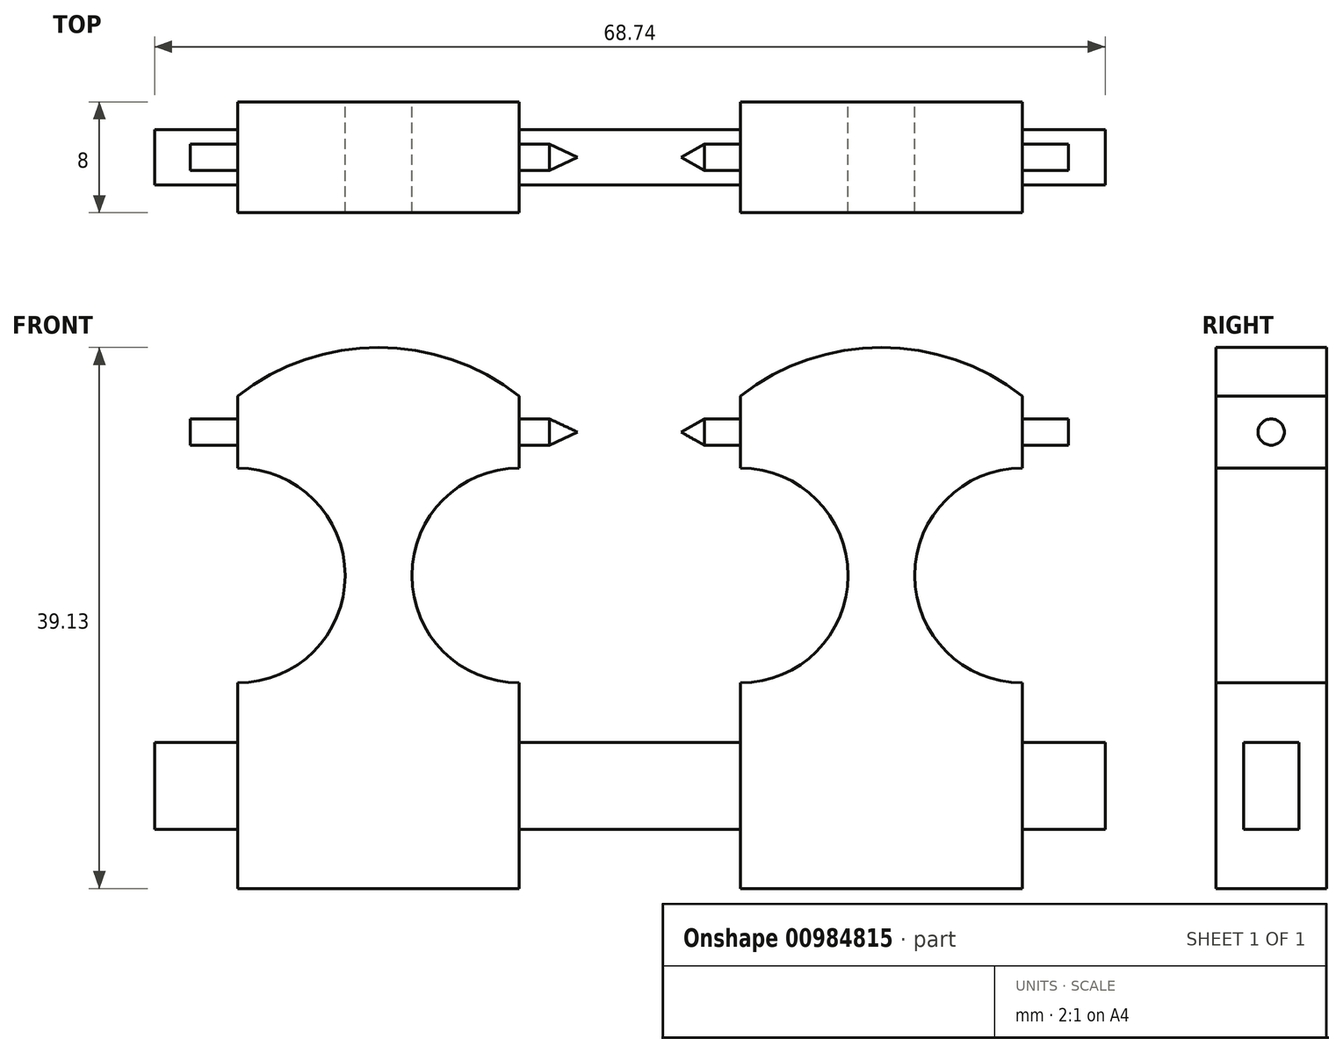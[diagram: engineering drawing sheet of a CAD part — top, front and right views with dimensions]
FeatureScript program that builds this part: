
annotation { "Feature Type Name" : "Feature", "Feature Type Description" : "" }
export const myFeature = defineFeature(function(context is Context, id is Id, definition is map)
    precondition{}
    {
        {
            var Q0;
            Q0=qCreatedBy(makeId("Front.planeOp"),FACE);
            var sketch = newSketch(context, id + "F0", { "sketchPlane" : qUnion([Q0])});
            skLineSegment(sketch, "E0", {"start": v(-34.37, 3.05) * mm, "end": v(-34.37, -3.23) * mm});
            skLineSegment(sketch, "E1", {"start": v(-34.37, -3.23) * mm, "end": v(-28.37, -3.23) * mm});
            skLineSegment(sketch, "E2", {"start": v(-28.37, -3.23) * mm, "end": v(-28.37, -7.5) * mm});
            skLineSegment(sketch, "E3", {"start": v(-28.37, -7.5) * mm, "end": v(-8, -7.5) * mm});
            skLineSegment(sketch, "E4", {"start": v(-8, -7.5) * mm, "end": v(-8, -3.23) * mm});
            skLineSegment(sketch, "E5", {"start": v(-8, -3.23) * mm, "end": v(8, -3.23) * mm});
            skLineSegment(sketch, "E6", {"start": v(8, -3.23) * mm, "end": v(8, -7.5) * mm});
            skLineSegment(sketch, "E7", {"start": v(8, -7.5) * mm, "end": v(28.37, -7.5) * mm});
            skLineSegment(sketch, "E8", {"start": v(28.37, -7.5) * mm, "end": v(28.37, -3.23) * mm});
            skLineSegment(sketch, "E9", {"start": v(28.37, -3.23) * mm, "end": v(34.37, -3.23) * mm});
            skLineSegment(sketch, "E10", {"start": v(34.37, -3.23) * mm, "end": v(34.37, 3.05) * mm});
            skLineSegment(sketch, "E11", {"start": v(34.37, 3.05) * mm, "end": v(28.37, 3.05) * mm});
            skLineSegment(sketch, "E12", {"start": v(28.37, 3.05) * mm, "end": v(28.37, 7.35) * mm});
            skLineSegment(sketch, "E13", {"start": v(-34.37, 3.05) * mm, "end": v(-28.37, 3.05) * mm});
            skLineSegment(sketch, "E14", {"start": v(-28.37, 3.05) * mm, "end": v(-28.37, 7.35) * mm});
            skLineSegment(sketch, "E15", {"start": v(-8, 7.35) * mm, "end": v(-8, 3.05) * mm});
            skLineSegment(sketch, "E16", {"start": v(-8, 3.05) * mm, "end": v(8, 3.05) * mm});
            skLineSegment(sketch, "E17", {"start": v(8, 3.05) * mm, "end": v(8, 7.35) * mm});
            skArc(sketch, "E18", {"start": v(-28.37, 7.35) * mm, "mid": v(-20.6, 15.12) * mm, "end": v(-28.37, 22.9) * mm});
            skArc(sketch, "E19", {"start": v(-8, 22.9) * mm, "mid": v(-15.77, 15.12) * mm, "end": v(-8, 7.35) * mm});
            skArc(sketch, "E20", {"start": v(8, 7.35) * mm, "mid": v(15.77, 15.12) * mm, "end": v(8, 22.9) * mm});
            skArc(sketch, "E21", {"start": v(28.37, 22.9) * mm, "mid": v(20.6, 15.12) * mm, "end": v(28.37, 7.35) * mm});
            skLineSegment(sketch, "E22", {"start": v(-28.37, 22.9) * mm, "end": v(-28.37, 28.1) * mm});
            skLineSegment(sketch, "E23", {"start": v(-8, 22.9) * mm, "end": v(-8, 28.1) * mm});
            skLineSegment(sketch, "E24", {"start": v(8, 22.9) * mm, "end": v(8, 28.1) * mm});
            skLineSegment(sketch, "E25", {"start": v(28.37, 22.9) * mm, "end": v(28.37, 28.1) * mm});
            skArc(sketch, "E26", {"start": v(-8, 28.1) * mm, "mid": v(-18.18, 31.62) * mm, "end": v(-28.37, 28.1) * mm});
            skArc(sketch, "E27", {"start": v(28.37, 28.1) * mm, "mid": v(18.18, 31.62) * mm, "end": v(8, 28.1) * mm});
            skLineSegment(sketch, "E28", {"start": v(-28.37, 3.05) * mm, "end": v(-28.37, -3.23) * mm});
            skLineSegment(sketch, "E29", {"start": v(-8, 3.05) * mm, "end": v(-8, -3.23) * mm});
            skLineSegment(sketch, "E30", {"start": v(8, 3.05) * mm, "end": v(8, -3.23) * mm});
            skLineSegment(sketch, "E31", {"start": v(28.37, 3.05) * mm, "end": v(28.37, -3.23) * mm});
            skLineSegment(sketch, "E32", {"start": v(-3.79, 25.5) * mm, "end": v(-5.82, 26.45) * mm});
            skPoint(sketch, "E32.startSnap0", {"position": v(-8, 25.5) * mm});
            skLineSegment(sketch, "E33", {"start": v(-5.82, 26.45) * mm, "end": v(-8, 26.45) * mm});
            skLineSegment(sketch, "E34", {"start": v(-8, 26.45) * mm, "end": v(-8, 24.44) * mm});
            skLineSegment(sketch, "E35", {"start": v(-8, 24.44) * mm, "end": v(-5.82, 24.44) * mm});
            skLineSegment(sketch, "E36", {"start": v(-5.82, 24.44) * mm, "end": v(-3.79, 25.5) * mm});
            skLineSegment(sketch, "E37", {"start": v(3.7, 25.5) * mm, "end": v(5.38, 24.44) * mm});
            skLineSegment(sketch, "E38", {"start": v(5.38, 24.44) * mm, "end": v(8, 24.44) * mm});
            skLineSegment(sketch, "E39", {"start": v(8, 24.44) * mm, "end": v(8, 26.45) * mm});
            skLineSegment(sketch, "E40", {"start": v(8, 26.45) * mm, "end": v(5.38, 26.45) * mm});
            skLineSegment(sketch, "E41", {"start": v(5.38, 26.45) * mm, "end": v(3.7, 25.5) * mm});
            skLineSegment(sketch, "E42.bottom", {"start": v(-28.37, 26.45) * mm, "end": v(-31.8, 26.45) * mm});
            skLineSegment(sketch, "E42.top", {"start": v(-28.37, 24.44) * mm, "end": v(-31.8, 24.44) * mm});
            skLineSegment(sketch, "E42.left", {"start": v(-28.37, 26.45) * mm, "end": v(-28.37, 24.44) * mm});
            skLineSegment(sketch, "E42.right", {"start": v(-31.8, 26.45) * mm, "end": v(-31.8, 24.44) * mm});
            skLineSegment(sketch, "E43.bottom", {"start": v(28.37, 26.45) * mm, "end": v(31.7, 26.45) * mm});
            skLineSegment(sketch, "E43.top", {"start": v(28.37, 24.44) * mm, "end": v(31.7, 24.44) * mm});
            skLineSegment(sketch, "E43.left", {"start": v(28.37, 26.45) * mm, "end": v(28.37, 24.44) * mm});
            skLineSegment(sketch, "E43.right", {"start": v(31.7, 26.45) * mm, "end": v(31.7, 24.44) * mm});
            skLineSegment(sketch, "E44", {"start": v(-3.79, 25.5) * mm, "end": v(-8, 25.5) * mm});
            skLineSegment(sketch, "E45", {"start": v(3.7, 25.5) * mm, "end": v(8, 25.5) * mm});
            skLineSegment(sketch, "E46", {"start": v(31.7, 25.5) * mm, "end": v(28.37, 25.5) * mm});
            skPoint(sketch, "E46.startSnap0", {"position": v(28.37, 25.5) * mm});
            skLineSegment(sketch, "E47", {"start": v(-31.8, 25.5) * mm, "end": v(-28.37, 25.5) * mm});
            skPoint(sketch, "E47.startSnap0", {"position": v(-28.37, 25.5) * mm});
            skSolve(sketch);
        }
        {
            var Q0;
            Q0=makeQuery(id+"F0.imprint","IMPRINT",FACE,{"disambiguationData":[TD([[makeQuery(id+"F0.imprint","IMPRINT",EDGE,{"derivedFrom":sQuery(id+"F0.wireOp",EDGE,"E2")}),1.0]])]});
            var Q1;
            Q1=makeQuery(id+"F0.imprint","IMPRINT",FACE,{"disambiguationData":[TD([[makeQuery(id+"F0.imprint","IMPRINT",EDGE,{"derivedFrom":sQuery(id+"F0.wireOp",EDGE,"E6")}),1.0]])]});
            extrude(context, id + "F1", {"entities" : qUnion([Q0, Q1]), "endBound" : BoundingType.SYMMETRIC, "depth" : 8 * mm, "offsetDistance" : 25 * mm});
        }
        {
            var Q0;
            Q0=makeQuery(id+"F0.imprint","IMPRINT",FACE,{"disambiguationData":[TD([[makeQuery(id+"F0.imprint","IMPRINT",EDGE,{"derivedFrom":sQuery(id+"F0.wireOp",EDGE,"E9")}),1.0]])]});
            var Q1;
            Q1=makeQuery(id+"F0.imprint","IMPRINT",FACE,{"disambiguationData":[TD([[makeQuery(id+"F0.imprint","IMPRINT",EDGE,{"derivedFrom":sQuery(id+"F0.wireOp",EDGE,"E5")}),1.0]])]});
            var Q2;
            Q2=makeQuery(id+"F0.imprint","IMPRINT",FACE,{"disambiguationData":[TD([[makeQuery(id+"F0.imprint","IMPRINT",EDGE,{"derivedFrom":sQuery(id+"F0.wireOp",EDGE,"E0")}),1.0]])]});
            extrude(context, id + "F2", {"entities" : qUnion([Q0, Q1, Q2]), "endBound" : BoundingType.SYMMETRIC, "depth" : 4 * mm, "offsetDistance" : 25 * mm});
        }
        {
            var Q0;
            Q0=makeQuery(id+"F0.imprint","IMPRINT",FACE,{"disambiguationData":[TD([[makeQuery(id+"F0.imprint","IMPRINT",EDGE,{"derivedFrom":sQuery(id+"F0.wireOp",EDGE,"E32")}),1.0]])]});
            var Q1;
            {var subQ0=sQuery(id+"F0.wireOp",EDGE,"E42.bottom");Q1=makeQuery(id+"F0.imprint","IMPRINT",FACE,{"disambiguationData":[TD([[makeQuery(id+"F0.imprint","IMPRINT",EDGE,{"derivedFrom":subQ0}),1.0]])]});}
            var Q2;
            {var subQ0=sQuery(id+"F0.wireOp",EDGE,"E40");Q2=makeQuery(id+"F0.imprint","IMPRINT",FACE,{"disambiguationData":[TD([[makeQuery(id+"F0.imprint","IMPRINT",EDGE,{"derivedFrom":subQ0}),1.0]])]});}
            var Q3;
            {var subQ0=sQuery(id+"F0.wireOp",EDGE,"E43.bottom");Q3=makeQuery(id+"F0.imprint","IMPRINT",FACE,{"disambiguationData":[TD([[makeQuery(id+"F0.imprint","IMPRINT",EDGE,{"derivedFrom":subQ0}),-1.0]])]});}
            var Q4;
            Q4=sQuery(id+"F0.wireOp",EDGE,"E44");
            revolve(context, id + "F3", {"surfaceOperationType" : NewSurfaceOperationType.NEW, "entities" : qUnion([Q0, Q1, Q2, Q3]), "axis" : qUnion([Q4]), "revolveType" : RevolveType.FULL});
        }
    });
